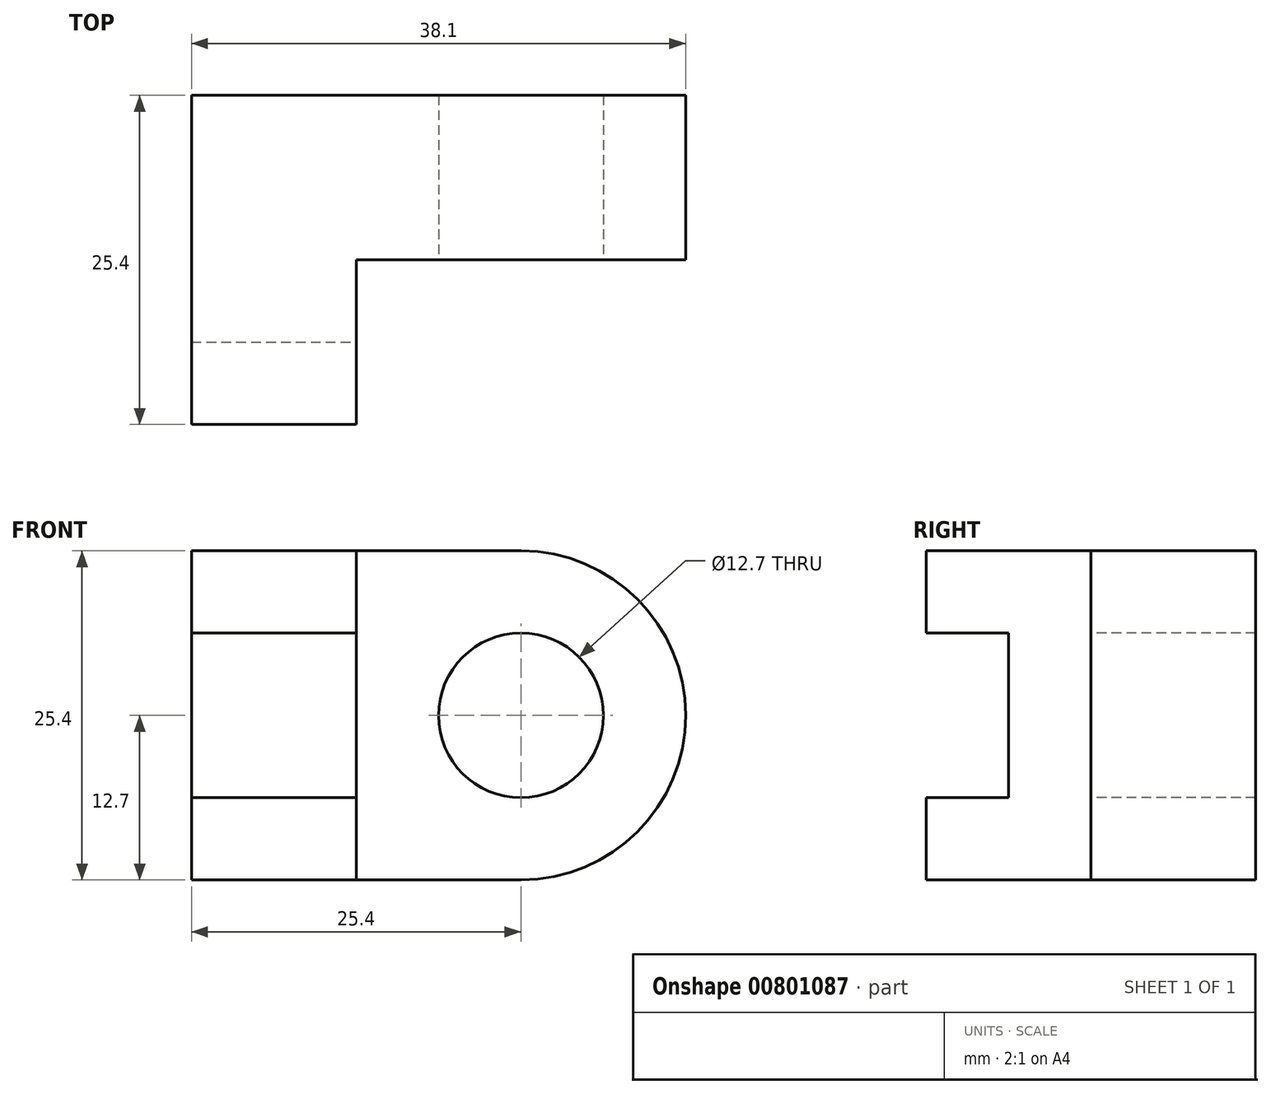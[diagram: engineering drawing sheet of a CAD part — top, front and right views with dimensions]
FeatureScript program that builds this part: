
annotation { "Feature Type Name" : "Feature", "Feature Type Description" : "" }
export const myFeature = defineFeature(function(context is Context, id is Id, definition is map)
    precondition{}
    {
        {
            var Q0;
            Q0=qCreatedBy(makeId("Top.planeOp"),FACE);
            var sketch = newSketch(context, id + "F0", { "sketchPlane" : qUnion([Q0])});
            skLineSegment(sketch, "E0", {"start": v(0, 0) * mm, "end": v(0, 25.4) * mm});
            skLineSegment(sketch, "E1", {"start": v(0, 25.4) * mm, "end": v(50.8, 25.4) * mm});
            skLineSegment(sketch, "E2", {"start": v(50.8, 25.4) * mm, "end": v(50.8, 12.7) * mm});
            skLineSegment(sketch, "E3", {"start": v(50.8, 12.7) * mm, "end": v(12.7, 12.7) * mm});
            skLineSegment(sketch, "E4", {"start": v(12.7, 12.7) * mm, "end": v(12.7, 0) * mm});
            skLineSegment(sketch, "E5", {"start": v(12.7, 0) * mm, "end": v(0, 0) * mm});
            skSolve(sketch);
        }
        {
            var Q0;
            Q0=makeQuery(id+"F0.imprint","IMPRINT",FACE,{"disambiguationData":[TD([[makeQuery(id+"F0.imprint","IMPRINT",EDGE,{"derivedFrom":sQuery(id+"F0.wireOp",EDGE,"E0")}),-1.0]])]});
            extrude(context, id + "F1", {"entities" : qUnion([Q0]), "depth" : 25.4 * mm, "offsetDistance" : 25.4 * mm});
        }
        {
            var Q0;
            Q0=makeQuery(id+"F1.opExtrude","SWEPT_FACE",FACE,{"disambiguationData":[OSD([sQuery(id+"F0.wireOp",EDGE,"E4")])]});
            var sketch = newSketch(context, id + "F2", { "sketchPlane" : qUnion([Q0])});
            skLineSegment(sketch, "E6", {"start": v(0, 25.4) * mm, "end": v(0, 19.05) * mm});
            skLineSegment(sketch, "E7", {"start": v(0, 19.05) * mm, "end": v(6.35, 19.05) * mm});
            skLineSegment(sketch, "E8", {"start": v(6.35, 19.05) * mm, "end": v(6.35, 6.35) * mm});
            skLineSegment(sketch, "E9", {"start": v(6.35, 6.35) * mm, "end": v(0, 6.35) * mm});
            skLineSegment(sketch, "E10", {"start": v(0, 6.35) * mm, "end": v(0, 0) * mm});
            skSolve(sketch);
        }
        {
            var Q0;
            {var subQ0=sQuery(id+"F2.wireOp",EDGE,"E7");Q0=makeQuery(id+"F2.imprint","IMPRINT",FACE,{"disambiguationData":[TD([[makeQuery(id+"F2.imprint","IMPRINT",EDGE,{"derivedFrom":subQ0}),-1.0]])]});}
            extrude(context, id + "F3", {"entities" : qUnion([Q0]), "operationType" : NewBodyOperationType.REMOVE, "oppositeDirection" : true, "depth" : 25.4 * mm, "offsetDistance" : 25.4 * mm});
        }
        {
            var Q0;
            Q0=makeQuery(id+"F1.opExtrude","SWEPT_FACE",FACE,{"disambiguationData":[OSD([sQuery(id+"F0.wireOp",EDGE,"E3")])]});
            var sketch = newSketch(context, id + "F4", { "sketchPlane" : qUnion([Q0])});
            skLineSegment(sketch, "E11", {"start": v(12.7, 25.4) * mm, "end": v(25.4, 25.4) * mm});
            skLineSegment(sketch, "E12", {"start": v(12.7, 0) * mm, "end": v(25.4, 0) * mm});
            skLineSegment(sketch, "E13", {"start": v(25.4, 25.4) * mm, "end": v(25.4, 0) * mm, "construction": true});
            skArc(sketch, "E14", {"start": v(25.4, 0) * mm, "mid": v(38.1, 12.7) * mm, "end": v(25.4, 25.4) * mm});
            skCircle(sketch, "E15", {"center": v(25.4, 12.7) * mm, "radius": 6.35 * mm});
            skSolve(sketch);
        }
        {
            var Q0;
            {var subQ0=sQuery(id+"F4.wireOp",EDGE,"E14");Q0=makeQuery(id+"F4.imprint","IMPRINT",FACE,{"disambiguationData":[TD([[makeQuery(id+"F4.imprint","IMPRINT",EDGE,{"derivedFrom":subQ0}),-1.0]])]});}
            extrude(context, id + "F5", {"entities" : qUnion([Q0]), "operationType" : NewBodyOperationType.REMOVE, "oppositeDirection" : true, "depth" : 25.4 * mm, "offsetDistance" : 25.4 * mm});
        }
        {
            var Q0;
            Q0=makeQuery(id+"F4.imprint","IMPRINT",FACE,{"disambiguationData":[TD([[makeQuery(id+"F4.imprint","IMPRINT",EDGE,{"derivedFrom":sQuery(id+"F4.wireOp",EDGE,"E15")}),1.0]])]});
            extrude(context, id + "F6", {"entities" : qUnion([Q0]), "operationType" : NewBodyOperationType.REMOVE, "oppositeDirection" : true, "depth" : 25.4 * mm, "offsetDistance" : 25.4 * mm});
        }
    });
